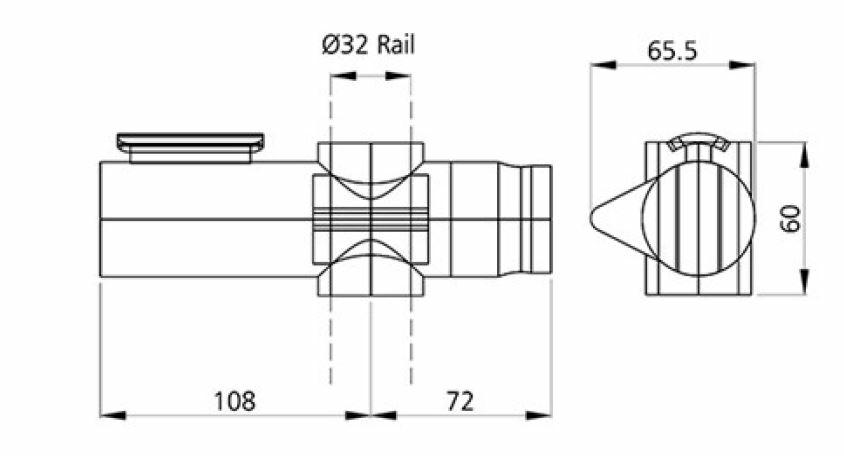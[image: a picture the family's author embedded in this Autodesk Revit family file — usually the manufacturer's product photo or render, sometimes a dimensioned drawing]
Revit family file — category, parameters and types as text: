
# Revit family: rba-bim-rba4110-950
name_source: partatom
category: Plumbing Fixtures
revit_build: Autodesk Revit 2018 (Build: 20170223_1515(x64)
units: mm (PartAtom-declared; Revit-internal decimal feet)

## family parameters
Always vertical = Yes
Cut with Voids When Loaded = No
Part Type = Normal
Room Calculation Point = No
Round Connector Dimension = Use Diameter
Shared = Yes
Work Plane-Based = No

## types (1)
- RBA4110-950
    CW Connection = Yes
    Description = RH T-Rail for Showers, incl Slider & 4 Star Handset and Mixer
    Distance Away from Toilet (default) = 1090 mm  [stored 3.57612 ft]
    Distance Away from Wall (default) = 100 mm  [stored 0.328084 ft]
    HW Connection = Yes
    Manufacturer = RBA Group
    Materials and Finishes = Chrome w/ Stainless Steel Hose
    Model = RBA4110-950
    Modified Issue = 20201014.01
    OFFSET = 1000 mm  [stored 3.28084 ft]
    URL = www.rba.com.au
    Vent Connection = Yes
    Waste Connection = Yes

note: [stored X ft] marks values corroborated as IEEE doubles in the binary element streams (Revit-internal decimal feet)

## geometry (parser evidence)
native form markers: Blend x20, Sweep x18
no freeform markers — native parametric forms only
